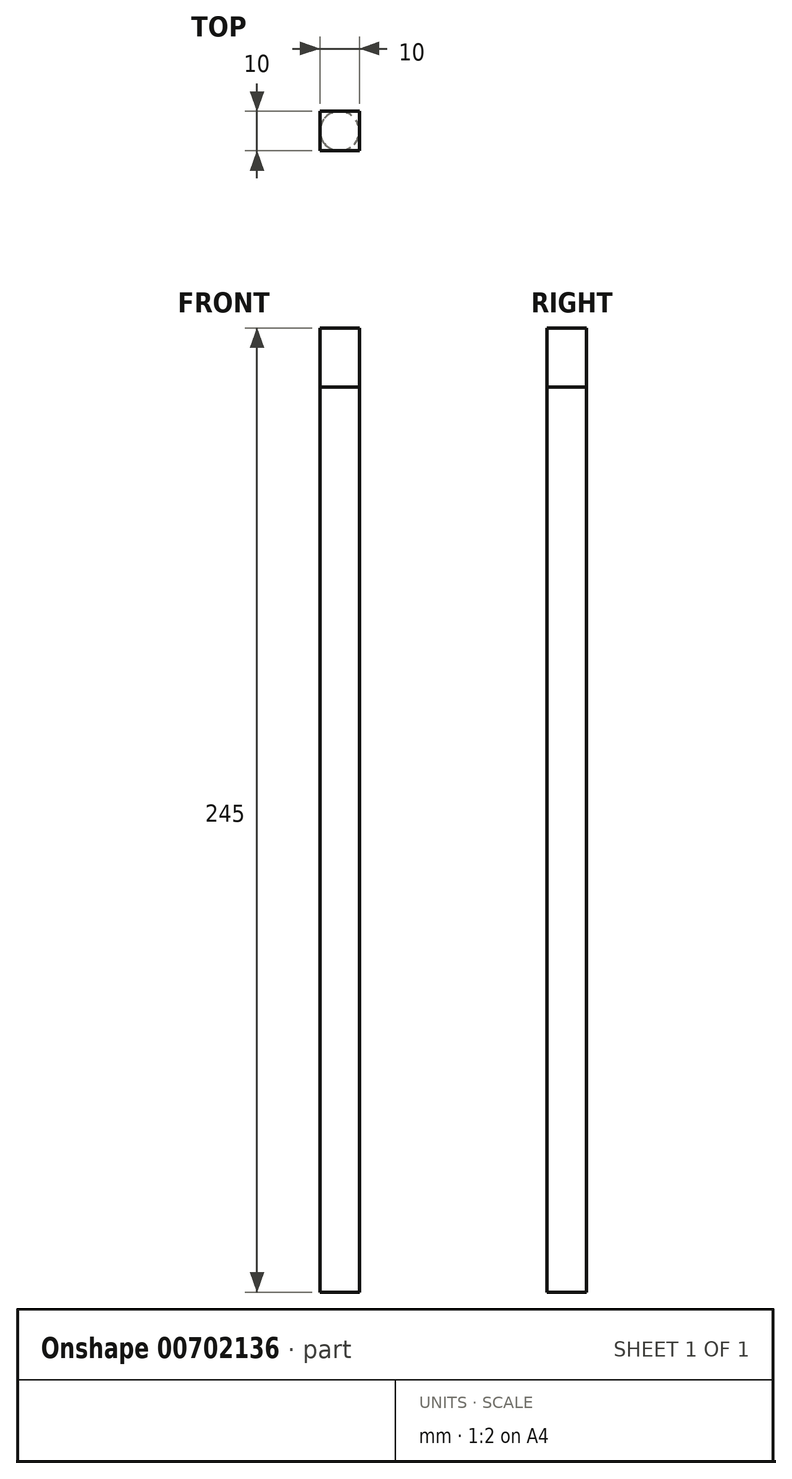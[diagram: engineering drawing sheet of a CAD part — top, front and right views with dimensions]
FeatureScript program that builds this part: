
annotation { "Feature Type Name" : "Feature", "Feature Type Description" : "" }
export const myFeature = defineFeature(function(context is Context, id is Id, definition is map)
    precondition{}
    {
        {
            var Q0;
            Q0=qCreatedBy(makeId("Top.planeOp"),FACE);
            var sketch = newSketch(context, id + "F0", { "sketchPlane" : qUnion([Q0])});
            skCircle(sketch, "E0", {"center": v(0, 0) * mm, "radius": 5 * mm});
            skSolve(sketch);
        }
        {
            var Q0;
            Q0=makeQuery(id+"F0.imprint","IMPRINT",FACE,{"disambiguationData":[TD([[makeQuery(id+"F0.imprint","IMPRINT",EDGE,{"derivedFrom":sQuery(id+"F0.wireOp",EDGE,"E0")}),1.0]])]});
            extrude(context, id + "F1", {"entities" : qUnion([Q0]), "depth" : 230 * mm, "offsetDistance" : 25 * mm});
        }
        {
            var Q0;
            Q0=makeQuery(id+"F1.opExtrude","CAP_FACE",FACE,{"disambiguationData":[OSD([sQuery(id+"F0.wireOp",EDGE,"E0")])],"isStart":false});
            var sketch = newSketch(context, id + "F2", { "sketchPlane" : qUnion([Q0])});
            skLineSegment(sketch, "E1.bottom", {"start": v(5, 5) * mm, "end": v(-5, 5) * mm});
            skLineSegment(sketch, "E1.top", {"start": v(5, -5) * mm, "end": v(-5, -5) * mm});
            skLineSegment(sketch, "E1.left", {"start": v(5, 5) * mm, "end": v(5, -5) * mm});
            skLineSegment(sketch, "E1.right", {"start": v(-5, 5) * mm, "end": v(-5, -5) * mm});
            skPoint(sketch, "E1.middle", {"position": v(0, 0) * mm});
            skSolve(sketch);
        }
        {
            var Q0;
            {var subQ0=sQuery(id+"F2.wireOp",EDGE,"E1.right");var subQ1=sQuery(id+"F2.wireOp",EDGE,"E1.bottom");var subQ2=makeQuery(id+"F2.imprint","INTERSECT",VERTEX,{"derivedFrom":[subQ1,subQ0]});Q0=makeQuery(id+"F2.imprint","IMPRINT",FACE,{"disambiguationData":[TD([[makeQuery(id+"F2.imprint","IMPRINT",EDGE,{"disambiguationData":[TD([[subQ2,1.0]])],"derivedFrom":subQ1}),1.0]])]});}
            var Q1;
            {var subQ0=sQuery(id+"F2.wireOp",EDGE,"E1.left");var subQ1=sQuery(id+"F2.wireOp",EDGE,"E1.bottom");var subQ2=makeQuery(id+"F2.imprint","INTERSECT",VERTEX,{"derivedFrom":[subQ1,subQ0]});Q1=makeQuery(id+"F2.imprint","IMPRINT",FACE,{"disambiguationData":[TD([[makeQuery(id+"F2.imprint","IMPRINT",EDGE,{"disambiguationData":[TD([[subQ2,-1.0]])],"derivedFrom":subQ1}),1.0]])]});}
            var Q2;
            {var subQ0=makeQuery(id+"F1.opExtrude","CAP_EDGE",EDGE,{"disambiguationData":[OSD([sQuery(id+"F0.wireOp",EDGE,"E0")])],"isStart":false});var subQ1=makeQuery(id+"F2.imprint","INTERSECT",VERTEX,{"derivedFrom":[subQ0,sQuery(id+"F2.wireOp",EDGE,"E1.bottom")]});Q2=makeQuery(id+"F2.imprint","IMPRINT",FACE,{"disambiguationData":[TD([[makeQuery(id+"F2.imprint","IMPRINT",EDGE,{"disambiguationData":[TD([[subQ1,1.0]])],"derivedFrom":subQ0}),1.0]])]});}
            var Q3;
            {var subQ0=sQuery(id+"F2.wireOp",EDGE,"E1.left");var subQ1=sQuery(id+"F2.wireOp",EDGE,"E1.top");var subQ2=makeQuery(id+"F2.imprint","INTERSECT",VERTEX,{"derivedFrom":[subQ1,subQ0]});Q3=makeQuery(id+"F2.imprint","IMPRINT",FACE,{"disambiguationData":[TD([[makeQuery(id+"F2.imprint","IMPRINT",EDGE,{"disambiguationData":[TD([[subQ2,-1.0]])],"derivedFrom":subQ1}),-1.0]])]});}
            var Q4;
            {var subQ0=sQuery(id+"F2.wireOp",EDGE,"E1.right");var subQ1=sQuery(id+"F2.wireOp",EDGE,"E1.top");var subQ2=makeQuery(id+"F2.imprint","INTERSECT",VERTEX,{"derivedFrom":[subQ1,subQ0]});Q4=makeQuery(id+"F2.imprint","IMPRINT",FACE,{"disambiguationData":[TD([[makeQuery(id+"F2.imprint","IMPRINT",EDGE,{"disambiguationData":[TD([[subQ2,1.0]])],"derivedFrom":subQ1}),-1.0]])]});}
            extrude(context, id + "F3", {"entities" : qUnion([Q0, Q1, Q2, Q3, Q4]), "operationType" : NewBodyOperationType.ADD, "depth" : 15 * mm, "offsetDistance" : 25 * mm});
        }
    });
